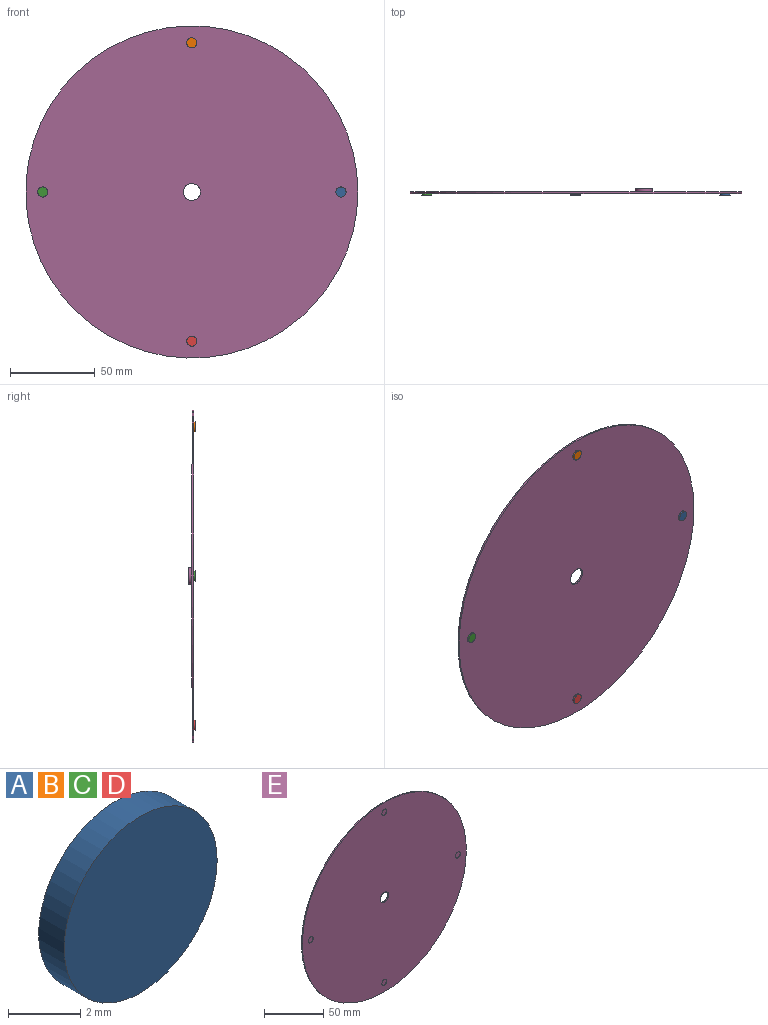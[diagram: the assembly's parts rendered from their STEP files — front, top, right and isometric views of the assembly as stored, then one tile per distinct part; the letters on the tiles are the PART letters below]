
ASSEMBLY  parts=5 mates=1
PART A: 3 faces, bbox 6x1x6 mm
  f0: cylinder r=3mm len=6mm, axis (0,1,0), area 18.8mm2, adj f1,f2
  f1: plane 6x6mm, normal (0,-1,0), area 28.3mm2, adj f0
  f2: plane 6x6mm, normal (0,1,0), area 28.3mm2, adj f0
PART B: same geometry as A
PART C: same geometry as A
PART D: same geometry as A
PART E: 16 faces, bbox 196x3x196 mm
  f0: cylinder r=5mm len=10mm, axis (0,1,0), area 31.4mm2, adj f2,f3
  f1: cylinder r=98mm len=196mm, axis (0,1,0), area 615.8mm2, adj f2,f3
  f2: plane 196x196mm, normal (0,-1,0), area 29980.2mm2, adj f0,f1,f8,f10,f12,f14
  f3: plane 196x196mm, normal (0,1,0), area 30014.8mm2, adj f0,f1,f6
  f4: plane 10x10mm, normal (0,1,0), area 50.3mm2, adj f5,f6
  f5: cylinder r=3mm len=6mm, axis (0,-1,0), area 37.7mm2, adj f4,f7
  f6: cylinder r=5mm len=10mm, axis (0,-1,0), area 62.8mm2, adj f3,f4
  f7: plane 6x6mm, normal (0,1,0), area 28.3mm2, adj f5
  f8: cylinder r=3mm len=6mm, axis (0,-1,0), area 9.4mm2, adj f2,f9
  f9: plane 6x6mm, normal (0,-1,0), area 28.3mm2, adj f8
  f10: cylinder r=3mm len=6mm, axis (0,-1,0), area 9.4mm2, adj f2,f11
  f11: plane 6x6mm, normal (0,-1,0), area 28.3mm2, adj f10
  f12: cylinder r=3mm len=6mm, axis (0,-1,0), area 9.4mm2, adj f2,f13
  f13: plane 6x6mm, normal (0,-1,0), area 28.3mm2, adj f12
  f14: cylinder r=3mm len=6mm, axis (0,-1,0), area 9.4mm2, adj f2,f15
  f15: plane 6x6mm, normal (0,-1,0), area 28.3mm2, adj f14
PLACE A rot(axis=(0,1,0),90deg) t=(0,-0.5,0)mm
PLACE B t=(0,-0.5,0)mm
PLACE C rot(axis=(0,-1,0),90deg) t=(0,-0.5,0)mm
PLACE D rot(axis=(0,-1,0),180deg) t=(0,-0.5,0)mm
PLACE E at identity fixed
MATE fastened E.f14 <-> B.f0  axis (0,-1,0) through (0,-19,88)mm
